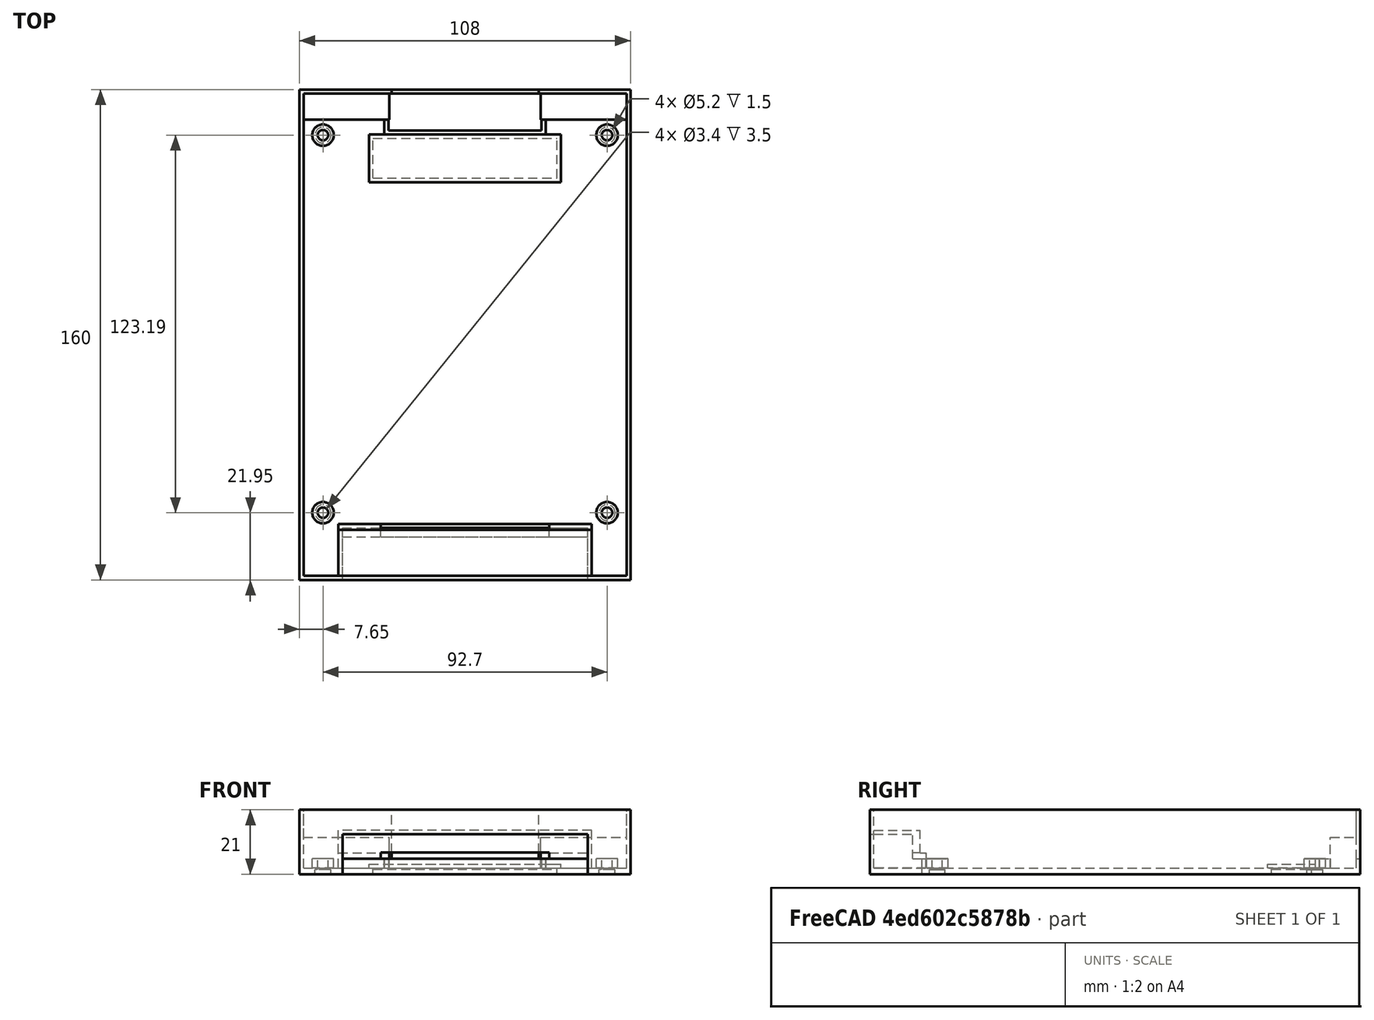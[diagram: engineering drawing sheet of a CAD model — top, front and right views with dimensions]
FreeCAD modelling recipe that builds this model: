
FCSTD DOCUMENT  (FreeCAD 0.18R4 (GitTag))
Label: DragonMMCBottom-v3
License: All rights reserved
LicenseURL: http://en.wikipedia.org/wiki/All_rights_reserved
objects: Part::Box×15, Part::Cut×10, Part::Cylinder×6, Part::MultiFuse×5, Part::FeaturePython×3
note: 39 computed .brp shape members not serialized (recipe doc carries the construction recipe); baked Part::Feature solids carry a one-line shape summary decoded from their .brp

FEATURE [Part::Box] Box  label="Cube"
  AttacherType = Attacher::AttachEngine3D
  Height = 21
  Length = 108
  Width = 160
FEATURE [Part::Box] Box001  label="Cube001"
  AttacherType = Attacher::AttachEngine3D
  Height = 19
  Length = 105.4
  Placement = pos=(1.3,1.3,2) rot=(0,0,1;0rad)
  Width = 157.4
FEATURE [Part::Cut] Cut  label="Outer Box"
  Base = -> Box
  Tool = -> Box001
FEATURE [Part::Box] Box002  label="Cube002"
  AttacherType = Attacher::AttachEngine3D
  Height = 13
  Length = 80
  Placement = pos=(14,0,0) rot=(0,0,1;0rad)
  Width = 17
FEATURE [Part::Cut] Cut001  label="Cartridge appature cutout"
  Base = -> Cut
  Tool = -> Box002
FEATURE [Part::Box] Box003  label="Appature"
  AttacherType = Attacher::AttachEngine3D
  Height = 14.3
  Length = 82.6
  Placement = pos=(12.7,0,0) rot=(0,0,1;0rad)
  Width = 18.3
FEATURE [Part::Box] Box004  label="Appature bottom outside carve"
  AttacherType = Attacher::AttachEngine3D
  Height = 5
  Length = 80
  Placement = pos=(14,0,0) rot=(0,0,1;0rad)
  Width = 17
FEATURE [Part::Cut] Cut002  label="AppatureC1"
  Base = -> Box003
  Tool = -> Box004
FEATURE [Part::Box] Box005  label="Appature top outside carve"
  AttacherType = Attacher::AttachEngine3D
  Height = 8
  Length = 80
  Placement = pos=(14,0,5) rot=(0,0,1;0rad)
  Width = 14
FEATURE [Part::Cut] Cut003  label="AppatureC2"
  Base = -> Cut002
  Tool = -> Box005
FEATURE [Part::Box] Box006  label="Appature top inside carve"
  AttacherType = Attacher::AttachEngine3D
  Height = 7.4
  Length = 82.6
  Placement = pos=(12.7,16.3,6.9) rot=(0,0,1;0rad)
  Width = 2
FEATURE [Part::Cut] Cut004  label="AppatureC3"
  Base = -> Cut003
  Tool = -> Box006
FEATURE [Part::Box] Box007  label="Board carve"
  AttacherType = Attacher::AttachEngine3D
  Height = 2
  Length = 55
  Placement = pos=(26.5,14,5) rot=(0,0,1;0rad)
  Width = 4.5
FEATURE [Part::Cut] Cut005  label="AppatureC4"
  Base = -> Cut004
  Tool = -> Box007
FEATURE [Part::Box] Box008  label="Bottom cutout"
  AttacherType = Attacher::AttachEngine3D
  Height = 1.6
  Length = 60
  Placement = pos=(24,131.1,0) rot=(0,0,1;0rad)
  Width = 13
FEATURE [Part::MultiFuse] Fusion  label="Case and appature"
  Shapes = -> [Cut005,Cut001]
FEATURE [Part::Cut] Cut006  label="Case with bottom cutout"
  Base = -> Fusion
  Tool = -> Box008
FEATURE [Part::Box] Box009  label="Bottomcutout cover"
  AttacherType = Attacher::AttachEngine3D
  Height = 1.7
  Length = 62.6
  Placement = pos=(22.7,129.8,1.6) rot=(0,0,1;0rad)
  Width = 15.6
FEATURE [Part::Box] Box012  label="SDCard cutout"
  AttacherType = Attacher::AttachEngine3D
  Height = 16
  Length = 48
  Placement = pos=(30,158.7,5) rot=(0,0,1;0rad)
  Width = 1.3
FEATURE [Part::Cut] Cut007  label="Case with SDCard cutout"
  Base = -> Cut006
  Tool = -> Box012
FEATURE [Part::Box] Box013  label="Board support outer"
  AttacherType = Attacher::AttachEngine3D
  Height = 3
  Length = 52.6
  Placement = pos=(27.7,145.4,2) rot=(0,0,1;0rad)
  Width = 14.6
FEATURE [Part::Box] Box014  label="Board support inner"
  AttacherType = Attacher::AttachEngine3D
  Height = 3
  Length = 50
  Placement = pos=(29,146.7,2) rot=(0,0,1;0rad)
  Width = 12
FEATURE [Part::Cut] Cut008  label="Board Support"
  Base = -> Box013
  Tool = -> Box014
FEATURE [Part::Cylinder] Cylinder  label="Board Post 1"
  Angle = 360
  AttacherType = Attacher::AttachEngine3D
  Height = 5
  Placement = pos=(7.65,145.14,0) rot=(0,0,1;0rad)
  Radius = 3.5
FEATURE [Part::Cylinder] Cylinder001  label="Board Post 2"
  Angle = 360
  AttacherType = Attacher::AttachEngine3D
  Height = 5
  Placement = pos=(100.35,145.14,0) rot=(0,0,1;0rad)
  Radius = 3.5
FEATURE [Part::Cylinder] Cylinder002  label="Board Post 3"
  Angle = 360
  AttacherType = Attacher::AttachEngine3D
  Height = 5
  Placement = pos=(7.65,21.95,0) rot=(0,0,1;0rad)
  Radius = 3.5
FEATURE [Part::Cylinder] Cylinder003  label="Board Post 4"
  Angle = 360
  AttacherType = Attacher::AttachEngine3D
  Height = 5
  Placement = pos=(100.35,21.95,0) rot=(0,0,1;0rad)
  Radius = 3.5
FEATURE [Part::Cylinder] Cylinder005  label="centre hole"
  Angle = 360
  AttacherType = Attacher::AttachEngine3D
  Height = 5
  Placement = pos=(7.65,145.14,0) rot=(0,0,1;0rad)
  Radius = 1.7
FEATURE [Part::Cylinder] Cylinder006  label="Bottom hole"
  Angle = 360
  AttacherType = Attacher::AttachEngine3D
  Height = 1.5
  Placement = pos=(7.65,145.14,0) rot=(0,0,1;0rad)
  Radius = 2.6
FEATURE [Part::MultiFuse] Fusion002  label="Case with mounting posts"
  Shapes = -> [Cut007,Cylinder,Cylinder001,Cylinder002,Cylinder003]
FEATURE [Part::MultiFuse] Fusion003  label="Hole1"
  Shapes = -> [Cylinder005,Cylinder006]
FEATURE [Part::FeaturePython] Clone  label="Hole2"  # Draft clone (typed FeaturePython)
  AttacherType = Attacher::AttachEngine3D
  Fuse = false
  Objects = -> [Fusion003]
  Placement = pos=(92.7,0,0) rot=(0,0,1;0rad)
  Scale = (1,1,1)
FEATURE [Part::FeaturePython] Clone001  label="Hole3"  # Draft clone (typed FeaturePython)
  AttacherType = Attacher::AttachEngine3D
  Fuse = false
  Objects = -> [Clone]
  Placement = pos=(0,-123.19,0) rot=(0,0,1;0rad)
  Scale = (1,1,1)
FEATURE [Part::FeaturePython] Clone002  label="Hole4"  # Draft clone (typed FeaturePython)
  AttacherType = Attacher::AttachEngine3D
  Fuse = false
  Objects = -> [Clone001]
  Placement = pos=(92.7,-123.19,0) rot=(0,0,1;0rad)
  Scale = (1,1,1)
FEATURE [Part::MultiFuse] Fusion004  label="Holes"
  Shapes = -> [Fusion003,Clone002,Clone001,Clone]
FEATURE [Part::Cut] Cut009  label="Board with holes"
  Base = -> Fusion002
  Tool = -> Fusion004
FEATURE [Part::Box] Box015  label="Board pusher left"
  AttacherType = Attacher::AttachEngine3D
  Height = 10
  Length = 28
  Placement = pos=(1.3,150.2,2) rot=(0,0,1;0rad)
  Width = 8.5
FEATURE [Part::Box] Box016  label="Board pusher right"
  AttacherType = Attacher::AttachEngine3D
  Height = 10
  Length = 28
  Placement = pos=(78.7,150.2,2) rot=(0,0,1;0rad)
  Width = 8.5
FEATURE [Part::MultiFuse] Fusion005  label="All case parts"
  Shapes = -> [Box009,Box015,Box016,Cut008,Cut009]
